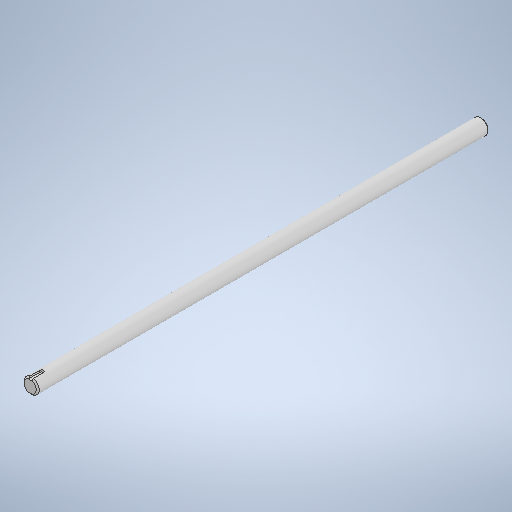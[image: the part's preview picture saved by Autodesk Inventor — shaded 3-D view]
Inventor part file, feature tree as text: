
AUTODESK INVENTOR PART (.ipt)
format: ipt  version: 2025.1 (Build 291241000, 241)  size: 269,824 bytes
history: native  units: in
note: dims shown in document units (in); Inventor stores cm internally (conversion verified against a paired STEP export)
features: extrude x2, sketch x2, chamfer x1, plane x1
ambient origin geometry x8: Origin, YZ Plane, XZ Plane, XY Plane, X Axis, Y Axis, Z Axis, Center Point
bodies: Solid1 (feature_tree)
feature tree (6):
  chamfer  "Chamfer1"  Distance=0.0625in
  plane  "Work Plane1"
  extrude  "Extrusion1"  Depth=0.0625in TaperAngle=0.0deg
  extrude  "Extrusion2"  [1 undecoded]
  sketch  "Sketch2"  dims[d0=0.125in]
  sketch  "Sketch3"  dims[d1=0.375in d2=0.0625in d3=0.0in d4=0.0625in d5=0.0in]
note: 1 required parameter value undecoded (feature->parameter linkage not recoverable at this tier; creation-order binding heuristic only, values carry confidence <= 0.55)
